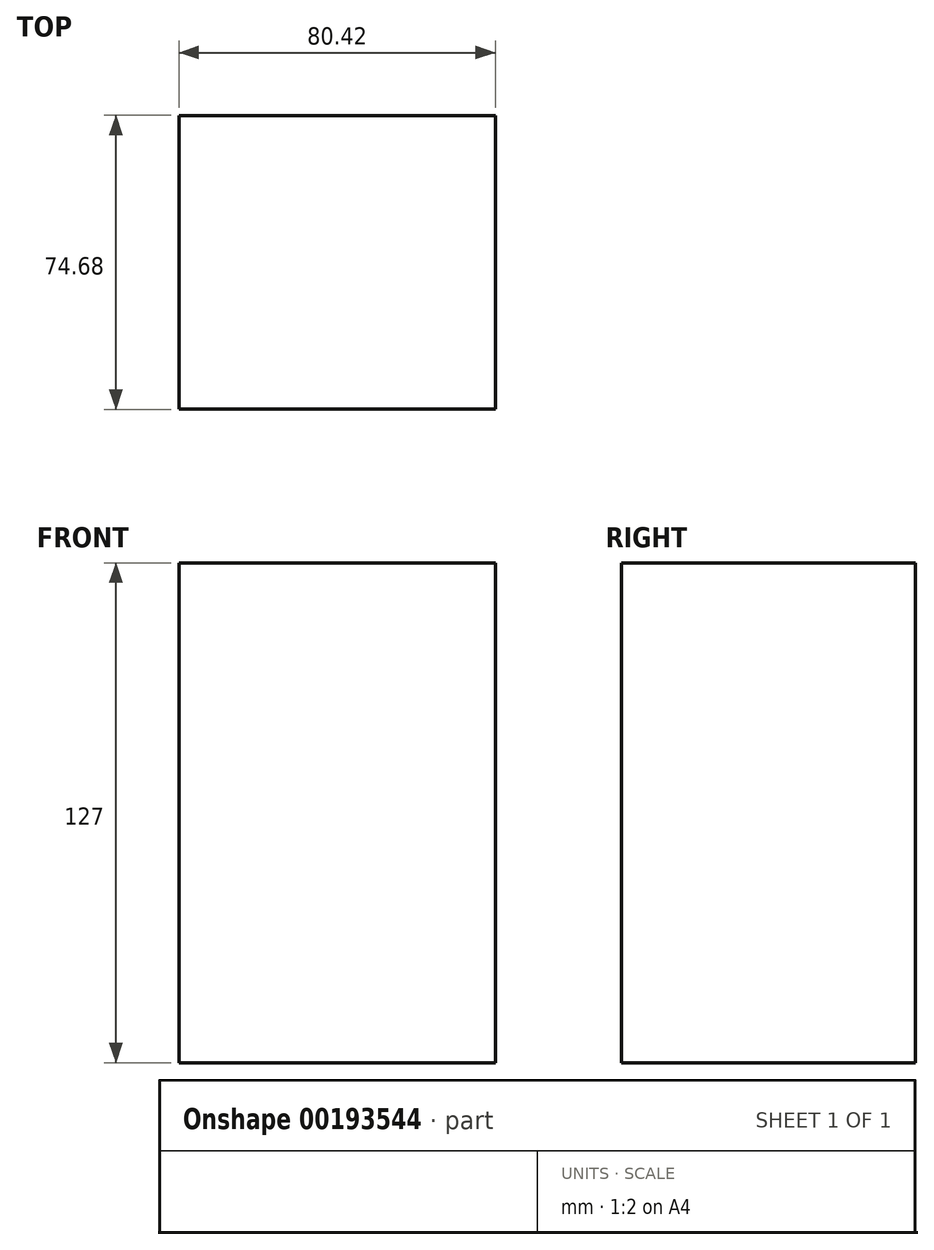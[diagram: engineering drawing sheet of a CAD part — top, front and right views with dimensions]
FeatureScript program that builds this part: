
annotation { "Feature Type Name" : "Feature", "Feature Type Description" : "" }
export const myFeature = defineFeature(function(context is Context, id is Id, definition is map)
    precondition{}
    {
        {
            var Q0;
            Q0=qCreatedBy(makeId("Top.planeOp"),FACE);
            var sketch = newSketch(context, id + "F0", { "sketchPlane" : qUnion([Q0])});
            skLineSegment(sketch, "E0.bottom", {"start": v(-40.2, 37.34) * mm, "end": v(40.2, 37.34) * mm});
            skLineSegment(sketch, "E0.top", {"start": v(-40.2, -37.34) * mm, "end": v(40.2, -37.34) * mm});
            skLineSegment(sketch, "E0.left", {"start": v(-40.2, 37.34) * mm, "end": v(-40.2, -37.34) * mm});
            skLineSegment(sketch, "E0.right", {"start": v(40.2, 37.34) * mm, "end": v(40.2, -37.34) * mm});
            skPoint(sketch, "E0.middle", {"position": v(0, 0) * mm});
            skSolve(sketch);
        }
        {
            var Q0;
            Q0 = qSketchRegion(id + "F0", true);
            extrude(context, id + "F1", {"entities" : qUnion([Q0]), "depth" : 127 * mm});
        }
    });
